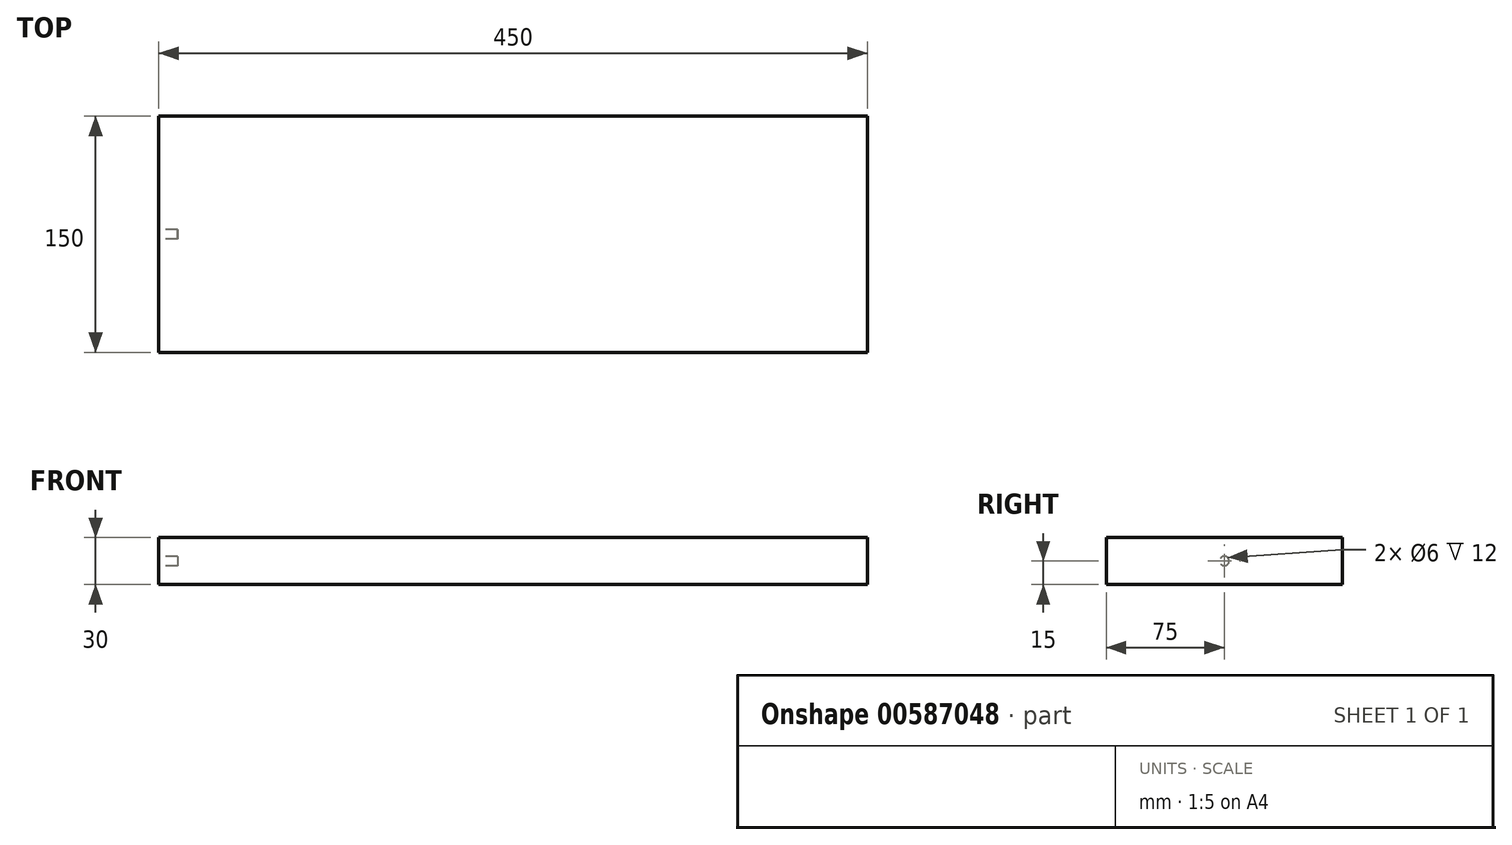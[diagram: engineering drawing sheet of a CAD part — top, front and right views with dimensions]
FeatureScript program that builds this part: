
annotation { "Feature Type Name" : "Feature", "Feature Type Description" : "" }
export const myFeature = defineFeature(function(context is Context, id is Id, definition is map)
    precondition{}
    {
        {
            var Q0;
            Q0=qCreatedBy(makeId("Top.planeOp"),FACE);
            var sketch = newSketch(context, id + "F0", { "sketchPlane" : qUnion([Q0])});
            skLineSegment(sketch, "E0.bottom", {"start": v(0, 0) * mm, "end": v(450, 0) * mm});
            skLineSegment(sketch, "E0.top", {"start": v(0, 150) * mm, "end": v(450, 150) * mm});
            skLineSegment(sketch, "E0.left", {"start": v(0, 0) * mm, "end": v(0, 150) * mm});
            skLineSegment(sketch, "E0.right", {"start": v(450, 0) * mm, "end": v(450, 150) * mm});
            skSolve(sketch);
        }
        {
            var Q0;
            Q0=makeQuery(id+"F0.imprint","IMPRINT",FACE,{"disambiguationData":[TD([[makeQuery(id+"F0.imprint","IMPRINT",EDGE,{"derivedFrom":sQuery(id+"F0.wireOp",EDGE,"E0.bottom")}),1.0]])]});
            extrude(context, id + "F1", {"entities" : qUnion([Q0]), "depth" : 30 * mm, "offsetDistance" : 25 * mm});
        }
        {
            var Q0;
            Q0=makeQuery(id+"F1.opExtrude","SWEPT_FACE",FACE,{"disambiguationData":[OSD([sQuery(id+"F0.wireOp",EDGE,"E0.left")])]});
            var sketch = newSketch(context, id + "F2", { "sketchPlane" : qUnion([Q0])});
            skCircle(sketch, "E1", {"center": v(-75, 15) * mm, "radius": 3 * mm});
            skPoint(sketch, "E1.centerSnap0", {"position": v(-75, 30) * mm});
            skPoint(sketch, "E1.centerSnap1", {"position": v(-150, 15) * mm});
            skSolve(sketch);
        }
        {
            var Q0;
            Q0=makeQuery(id+"F2.imprint","IMPRINT",FACE,{"disambiguationData":[TD([[makeQuery(id+"F2.imprint","IMPRINT",EDGE,{"derivedFrom":sQuery(id+"F2.wireOp",EDGE,"E1")}),1.0]])]});
            extrude(context, id + "F3", {"entities" : qUnion([Q0]), "operationType" : NewBodyOperationType.REMOVE, "oppositeDirection" : true, "depth" : 12 * mm, "offsetDistance" : 25 * mm});
        }
    });
